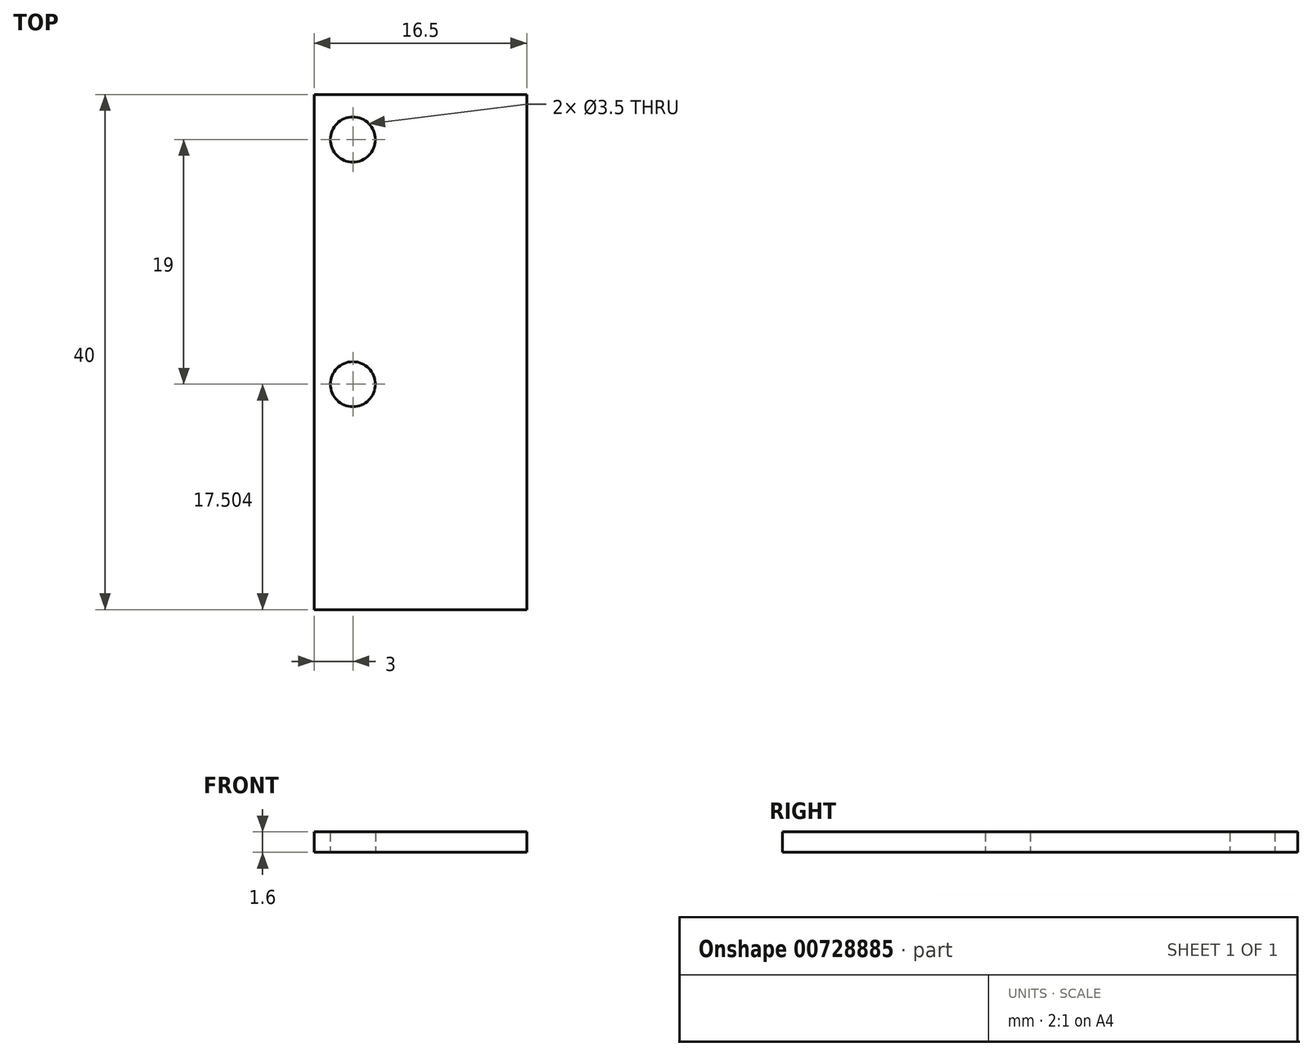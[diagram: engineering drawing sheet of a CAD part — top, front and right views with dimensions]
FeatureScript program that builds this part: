
annotation { "Feature Type Name" : "Feature", "Feature Type Description" : "" }
export const myFeature = defineFeature(function(context is Context, id is Id, definition is map)
    precondition{}
    {
        {
            var Q0;
            Q0=qCreatedBy(makeId("Top.planeOp"),FACE);
            var sketch = newSketch(context, id + "F0", { "sketchPlane" : qUnion([Q0])});
            skLineSegment(sketch, "E0.bottom", {"start": v(-26.68, 17.43) * mm, "end": v(-10.18, 17.43) * mm});
            skLineSegment(sketch, "E0.top", {"start": v(-26.68, -22.57) * mm, "end": v(-10.18, -22.57) * mm});
            skLineSegment(sketch, "E0.left", {"start": v(-26.68, 17.43) * mm, "end": v(-26.68, -22.57) * mm});
            skLineSegment(sketch, "E0.right", {"start": v(-10.18, 17.43) * mm, "end": v(-10.18, -22.57) * mm});
            skCircle(sketch, "E1", {"center": v(-23.68, 13.93) * mm, "radius": 1.75 * mm});
            skCircle(sketch, "E2", {"center": v(-23.68, -5.07) * mm, "radius": 1.75 * mm});
            skSolve(sketch);
        }
        {
            var Q0;
            Q0=makeQuery(id+"F0.imprint","IMPRINT",FACE,{"disambiguationData":[TD([[makeQuery(id+"F0.imprint","IMPRINT",EDGE,{"derivedFrom":sQuery(id+"F0.wireOp",EDGE,"E0.bottom")}),-1.0]])]});
            extrude(context, id + "F1", {"entities" : qUnion([Q0]), "depth" : 1.6 * mm, "offsetDistance" : 25 * mm});
        }
    });
